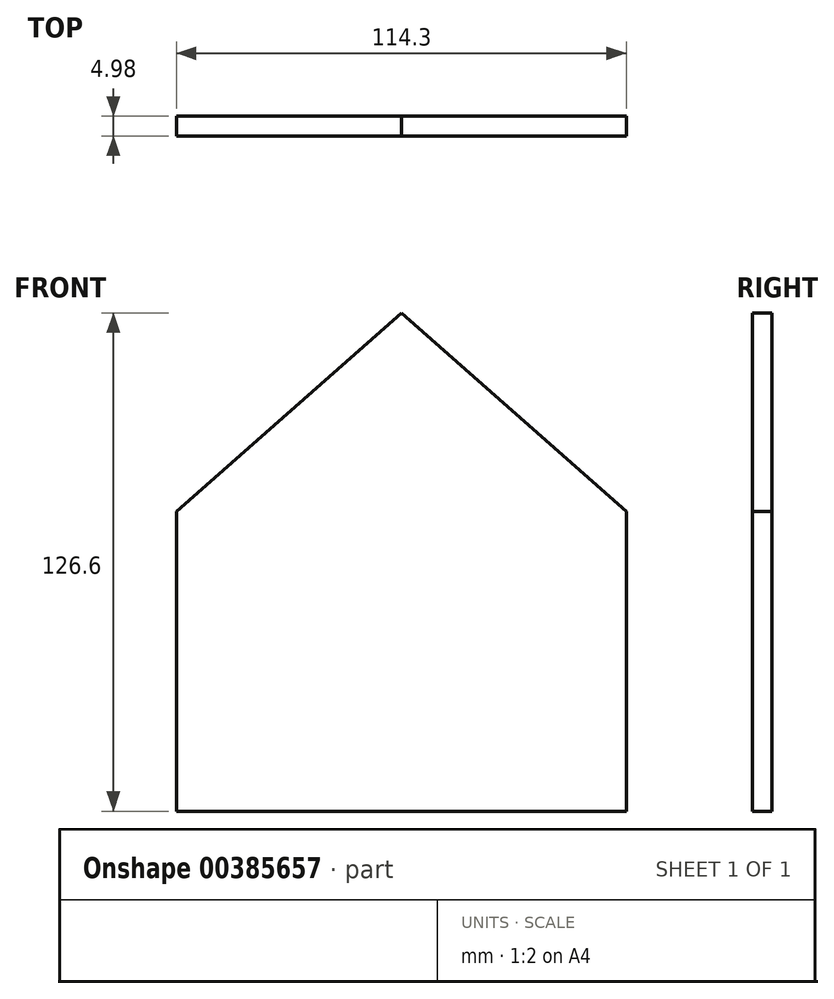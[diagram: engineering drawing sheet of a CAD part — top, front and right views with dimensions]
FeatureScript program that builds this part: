
annotation { "Feature Type Name" : "Feature", "Feature Type Description" : "" }
export const myFeature = defineFeature(function(context is Context, id is Id, definition is map)
    precondition{}
    {
        {
            var Q0;
            Q0=qCreatedBy(makeId("Front.planeOp"),FACE);
            var sketch = newSketch(context, id + "F0", { "sketchPlane" : qUnion([Q0])});
            skLineSegment(sketch, "E0.bottom", {"start": v(57.15, 38.1) * mm, "end": v(-57.15, 38.1) * mm});
            skLineSegment(sketch, "E0.top", {"start": v(57.15, -38.1) * mm, "end": v(-57.15, -38.1) * mm});
            skLineSegment(sketch, "E0.left", {"start": v(57.15, 38.1) * mm, "end": v(57.15, -38.1) * mm});
            skLineSegment(sketch, "E0.right", {"start": v(-57.15, 38.1) * mm, "end": v(-57.15, -38.1) * mm});
            skPoint(sketch, "E0.middle", {"position": v(0, 0) * mm});
            skLineSegment(sketch, "E1", {"start": v(-57.15, 38.1) * mm, "end": v(0, 88.5) * mm});
            skLineSegment(sketch, "E2", {"start": v(0, 88.5) * mm, "end": v(57.15, 38.1) * mm});
            skSolve(sketch);
        }
        {
            var Q0;
            Q0=qSketchRegion(id+"F0",true);
            extrude(context, id + "F1", {"entities" : qUnion([Q0]), "depth" : 4.98 * mm});
        }
    });
